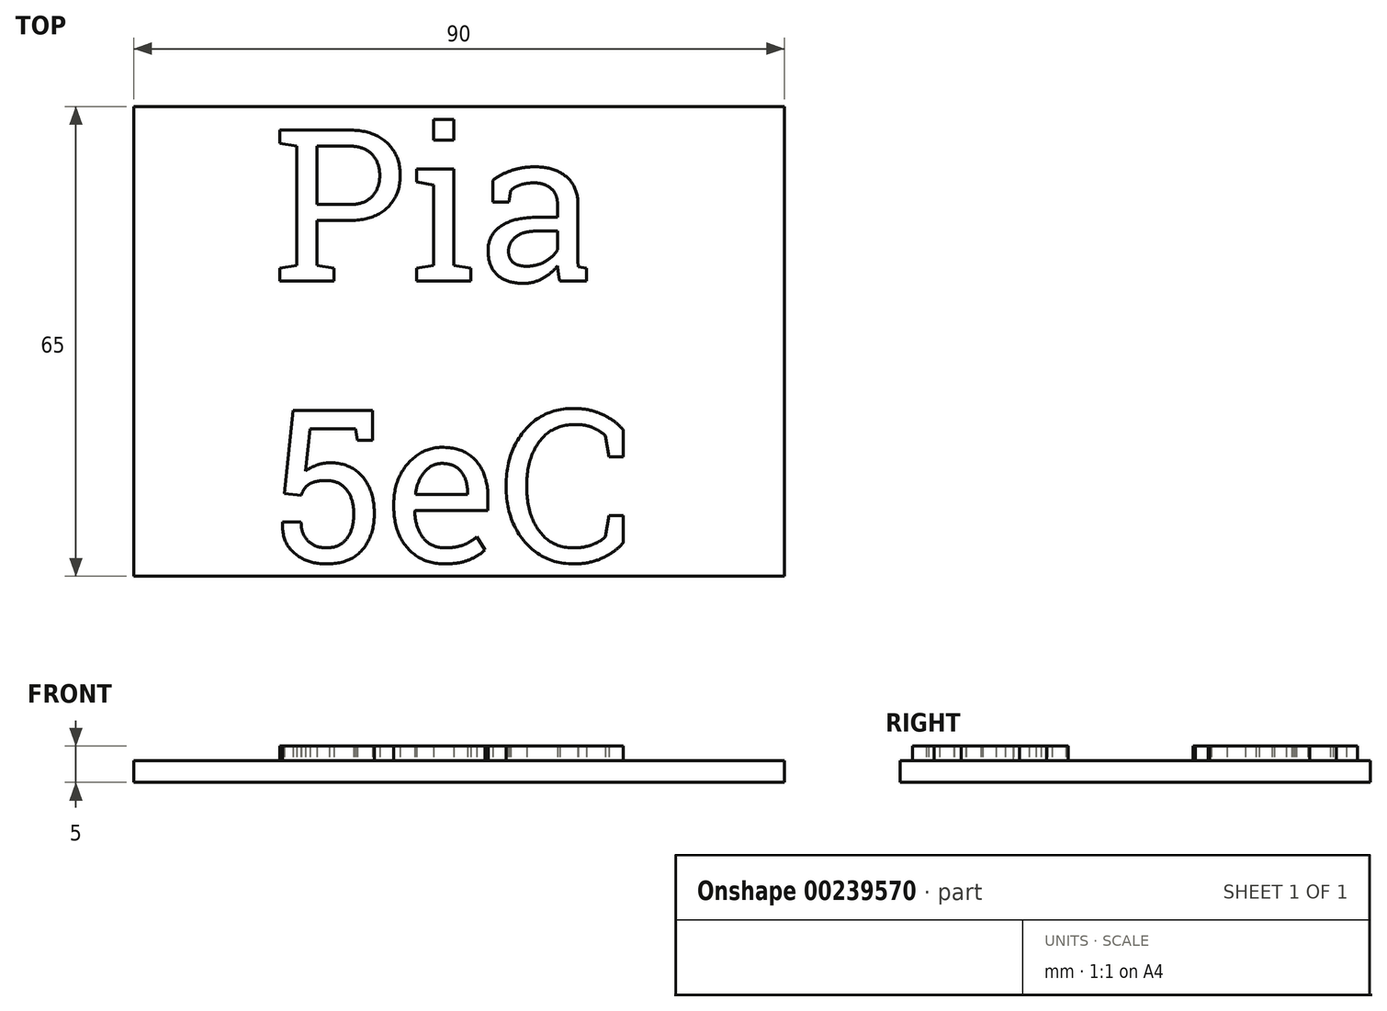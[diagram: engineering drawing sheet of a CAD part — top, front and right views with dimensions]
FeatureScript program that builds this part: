
annotation { "Feature Type Name" : "Feature", "Feature Type Description" : "" }
export const myFeature = defineFeature(function(context is Context, id is Id, definition is map)
    precondition{}
    {
        {
            var Q0;
            Q0=qCreatedBy(makeId("Top.planeOp"),FACE);
            var sketch = newSketch(context, id + "F0", { "sketchPlane" : qUnion([Q0])});
            skLineSegment(sketch, "E0.bottom", {"start": v(0, 0) * mm, "end": v(90, 0) * mm});
            skLineSegment(sketch, "E0.top", {"start": v(0, -65) * mm, "end": v(90, -65) * mm});
            skLineSegment(sketch, "E0.left", {"start": v(0, 0) * mm, "end": v(0, -65) * mm});
            skLineSegment(sketch, "E0.right", {"start": v(90, 0) * mm, "end": v(90, -65) * mm});
            skSolve(sketch);
        }
        {
            var Q0;
            Q0=makeQuery(id+"F0.imprint","IMPRINT",FACE,{"disambiguationData":[TD([[makeQuery(id+"F0.imprint","IMPRINT",EDGE,{"derivedFrom":sQuery(id+"F0.wireOp",EDGE,"E0.bottom")}),-1.0]])]});
            extrude(context, id + "F1", {"entities" : qUnion([Q0]), "depth" : 3 * mm});
        }
        {
            var Q0;
            Q0=makeQuery(id+"F1.opExtrude","CAP_FACE",FACE,{"disambiguationData":[OSD([sQuery(id+"F0.wireOp",EDGE,"E0.bottom"),sQuery(id+"F0.wireOp",EDGE,"E0.top"),sQuery(id+"F0.wireOp",EDGE,"E0.left"),sQuery(id+"F0.wireOp",EDGE,"E0.right")])],"isStart":false});
            var sketch = newSketch(context, id + "F2", { "sketchPlane" : qUnion([Q0])});
            skText(sketch, "E1", { "text": "  Pia \n  5eC", "fontName": "RobotoSlab-Regular.ttf"});
            const initialGuessF2  = {"E1": [0.00456, -0.02417, 1, 0, 0.02117]};
            skSetInitialGuess(sketch, initialGuessF2);
            skSolve(sketch);
        }
        {
            var Q0;
            Q0 = qSketchRegion(id + "F2", true);
            extrude(context, id + "F3", {"entities" : qUnion([Q0]), "operationType" : NewBodyOperationType.ADD, "depth" : 2 * mm});
        }
    });
